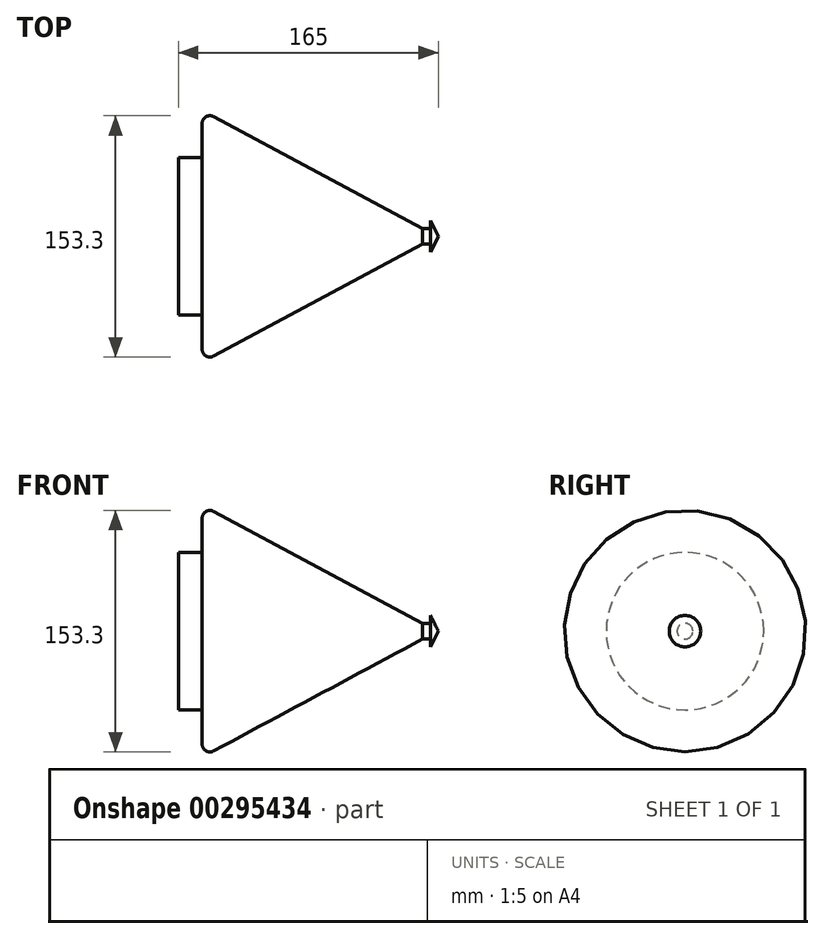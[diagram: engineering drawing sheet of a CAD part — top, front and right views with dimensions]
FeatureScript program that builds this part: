
annotation { "Feature Type Name" : "Feature", "Feature Type Description" : "" }
export const myFeature = defineFeature(function(context is Context, id is Id, definition is map)
    precondition{}
    {
        {
            var Q0;
            Q0=qCreatedBy(makeId("Top.planeOp"),FACE);
            var sketch = newSketch(context, id + "F0", { "sketchPlane" : qUnion([Q0])});
            skLineSegment(sketch, "E0", {"start": v(-386.3, 0) * mm, "end": v(-386.3, 50) * mm});
            skLineSegment(sketch, "E1", {"start": v(-386.3, 50) * mm, "end": v(-371.3, 50) * mm});
            skLineSegment(sketch, "E2", {"start": v(-371.3, 50) * mm, "end": v(-371.3, 71.65) * mm});
            skLineSegment(sketch, "E3", {"start": v(-429.84, 0) * mm, "end": v(-279.84, 0) * mm, "construction": true});
            skLineSegment(sketch, "E4", {"start": v(-221.3, 0) * mm, "end": v(-386.3, 0) * mm});
            skLineSegment(sketch, "E5", {"start": v(-363.93, 76.06) * mm, "end": v(-231.3, 5) * mm});
            skLineSegment(sketch, "E6", {"start": v(-231.3, 5) * mm, "end": v(-226.3, 5) * mm});
            skLineSegment(sketch, "E7", {"start": v(-226.3, 5) * mm, "end": v(-226.3, 10) * mm});
            skLineSegment(sketch, "E8", {"start": v(-232.97, 0) * mm, "end": v(-386.3, 0) * mm});
            skLineSegment(sketch, "E9", {"start": v(-221.3, 0) * mm, "end": v(-226.3, 10) * mm});
            skPoint(sketch, "E10.visualSharp", {"position": v(-371.3, 80) * mm});
            skArc(sketch, "E10.filletArc", {"start": v(-363.93, 76.06) * mm, "mid": v(-368.86, 75.94) * mm, "end": v(-371.3, 71.65) * mm});
            skSolve(sketch);
        }
        {
            var Q0;
            Q0=makeQuery(id+"F0.imprint","IMPRINT",FACE,{"disambiguationData":[TD([[makeQuery(id+"F0.imprint","IMPRINT",EDGE,{"derivedFrom":sQuery(id+"F0.wireOp",EDGE,"E0")}),-1.0]])]});
            var Q1;
            Q1=sQuery(id+"F0.wireOp",EDGE,"E8");
            revolve(context, id + "F1", {"entities" : qUnion([Q0]), "axis" : qUnion([Q1]), "revolveType" : RevolveType.FULL});
        }
    });
